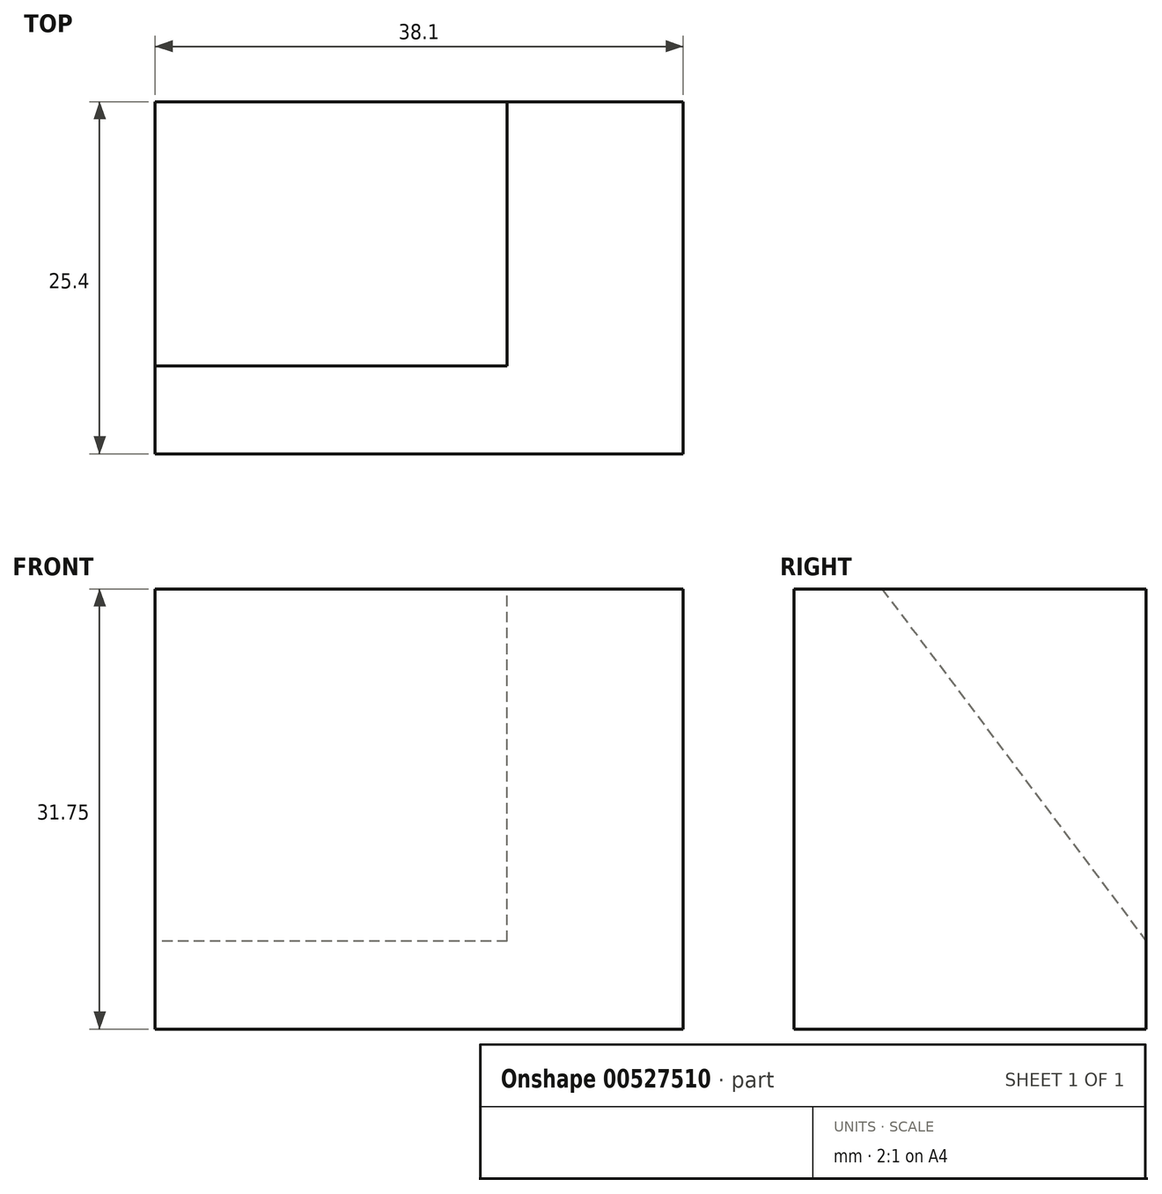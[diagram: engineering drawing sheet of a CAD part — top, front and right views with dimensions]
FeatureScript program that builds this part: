
annotation { "Feature Type Name" : "Feature", "Feature Type Description" : "" }
export const myFeature = defineFeature(function(context is Context, id is Id, definition is map)
    precondition{}
    {
        {
            var Q0;
            Q0=qCreatedBy(makeId("Front.planeOp"),FACE);
            var sketch = newSketch(context, id + "F0", { "sketchPlane" : qUnion([Q0])});
            skLineSegment(sketch, "E0", {"start": v(0, 0) * mm, "end": v(0, 31.75) * mm});
            skLineSegment(sketch, "E1", {"start": v(0, 31.75) * mm, "end": v(38.1, 31.75) * mm});
            skLineSegment(sketch, "E2", {"start": v(38.1, 31.75) * mm, "end": v(38.1, 0) * mm});
            skLineSegment(sketch, "E3", {"start": v(38.1, 0) * mm, "end": v(0, 0) * mm});
            skSolve(sketch);
        }
        {
            var Q0;
            Q0=makeQuery(id+"F0.imprint","IMPRINT",FACE,{"disambiguationData":[TD([[makeQuery(id+"F0.imprint","IMPRINT",EDGE,{"derivedFrom":sQuery(id+"F0.wireOp",EDGE,"E0")}),-1.0]])]});
            extrude(context, id + "F1", {"entities" : qUnion([Q0]), "depth" : 25.4 * mm, "offsetDistance" : 25.4 * mm});
        }
        {
            var Q0;
            Q0=qCreatedBy(makeId("Right.planeOp"),FACE);
            var sketch = newSketch(context, id + "F2", { "sketchPlane" : qUnion([Q0])});
            skLineSegment(sketch, "E4", {"start": v(0, 0) * mm, "end": v(0, 6.35) * mm});
            skLineSegment(sketch, "E5", {"start": v(0, 25.54) * mm, "end": v(0, 6.35) * mm});
            skLineSegment(sketch, "E6", {"start": v(0, 6.35) * mm, "end": v(0, 31.75) * mm});
            skLineSegment(sketch, "E7", {"start": v(0, 31.75) * mm, "end": v(-19.05, 31.75) * mm});
            skLineSegment(sketch, "E8", {"start": v(0, 6.35) * mm, "end": v(-19.05, 31.75) * mm});
            skSolve(sketch);
        }
        {
            var Q0;
            {var subQ2=sQuery(id+"F2.wireOp",EDGE,"E7");Q0=makeQuery(id+"F2.imprint","IMPRINT",FACE,{"disambiguationData":[TD([[makeQuery(id+"F2.imprint","IMPRINT",EDGE,{"derivedFrom":subQ2}),1.0]])]});}
            extrude(context, id + "F3", {"entities" : qUnion([Q0]), "operationType" : NewBodyOperationType.REMOVE, "oppositeDirection" : true, "depth" : 19.05 * mm, "offsetDistance" : 25.4 * mm});
        }
        {
            var Q0;
            Q0=makeQuery(id+"F1.opExtrude","SWEPT_FACE",FACE,{"disambiguationData":[OSD([sQuery(id+"F0.wireOp",EDGE,"E0")])]});
            var sketch = newSketch(context, id + "F4", { "sketchPlane" : qUnion([Q0])});
            skLineSegment(sketch, "E9", {"start": v(19.05, 31.75) * mm, "end": v(0, 6.35) * mm});
            skLineSegment(sketch, "E10", {"start": v(19.05, 31.75) * mm, "end": v(25.4, 31.75) * mm});
            skLineSegment(sketch, "E11", {"start": v(0, 6.35) * mm, "end": v(0, 0) * mm});
            skSolve(sketch);
        }
        {
            var Q0;
            {var subQ0=sQuery(id+"F4.wireOp",EDGE,"E9");Q0=makeQuery(id+"F4.imprint","IMPRINT",FACE,{"disambiguationData":[TD([[makeQuery(id+"F4.imprint","IMPRINT",EDGE,{"derivedFrom":subQ0}),-1.0]])]});}
            extrude(context, id + "F5", {"entities" : qUnion([Q0]), "operationType" : NewBodyOperationType.REMOVE, "oppositeDirection" : true, "depth" : 25.4 * mm, "offsetDistance" : 25.4 * mm});
        }
    });
